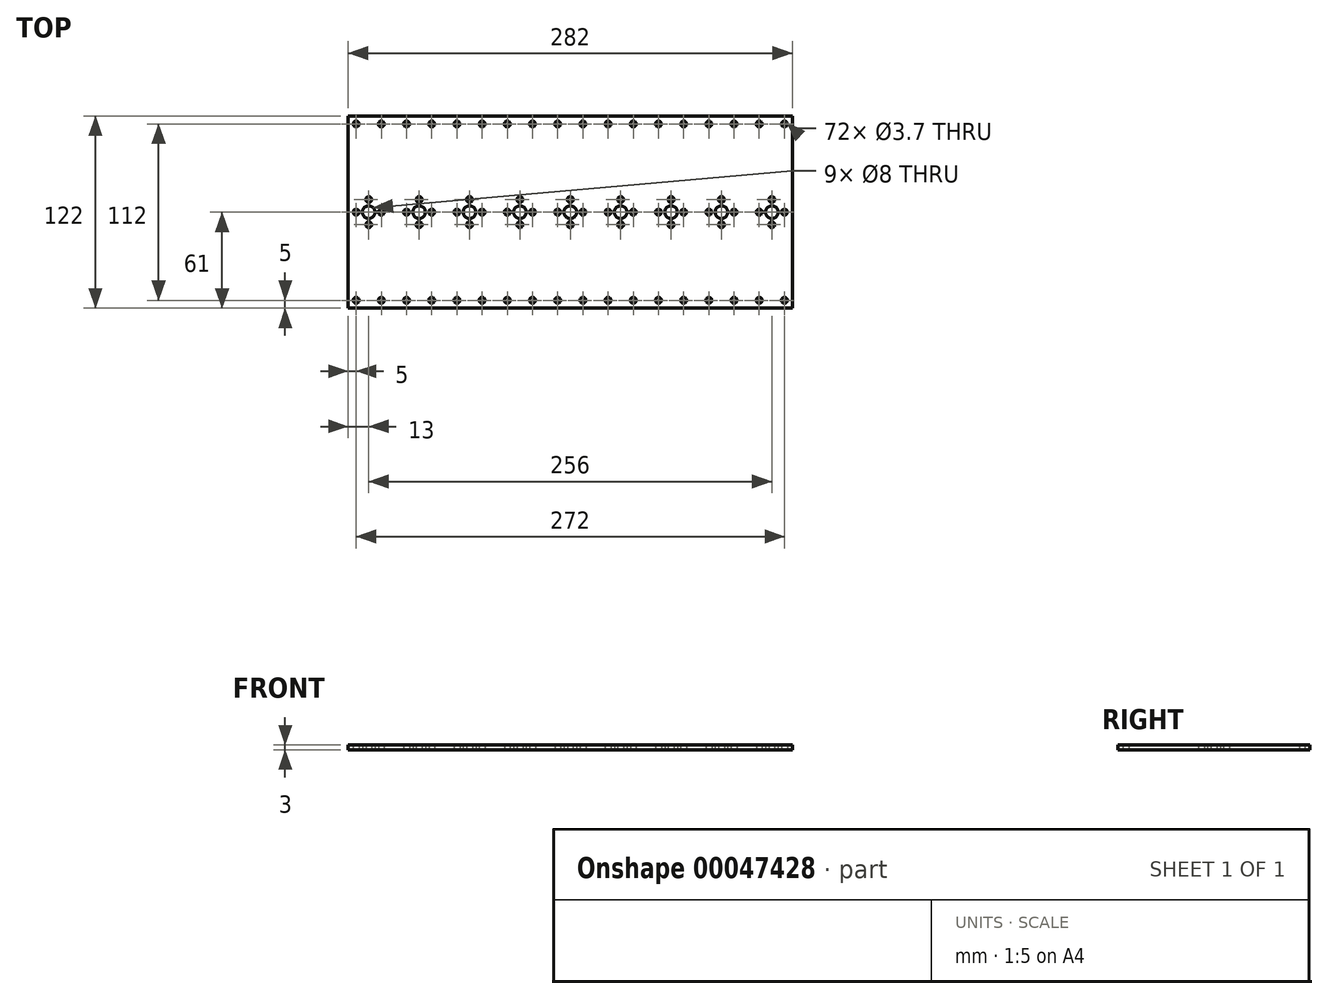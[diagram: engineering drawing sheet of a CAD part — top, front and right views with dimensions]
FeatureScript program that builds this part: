
annotation { "Feature Type Name" : "Feature", "Feature Type Description" : "" }
export const myFeature = defineFeature(function(context is Context, id is Id, definition is map)
    precondition{}
    {
        {
            var Q0;
            Q0=qCreatedBy(makeId("Top.planeOp"),FACE);
            var sketch = newSketch(context, id + "F0", { "sketchPlane" : qUnion([Q0])});
            skLineSegment(sketch, "E0.rect.bottom", {"start": v(-141, -61) * mm, "end": v(141, -61) * mm});
            skLineSegment(sketch, "E0.rect.top", {"start": v(-141, 61) * mm, "end": v(141, 61) * mm});
            skLineSegment(sketch, "E0.rect.left", {"start": v(-141, -61) * mm, "end": v(-141, 61) * mm});
            skLineSegment(sketch, "E0.rect.right", {"start": v(141, -61) * mm, "end": v(141, 61) * mm});
            skPoint(sketch, "E0.rect.middle", {"position": v(0, 0) * mm});
            skCircle(sketch, "E1", {"center": v(0, 0) * mm, "radius": 4 * mm});
            skCircle(sketch, "E2", {"center": v(0, -8) * mm, "radius": 1.85 * mm});
            skCircle(sketch, "E3.1.0", {"center": v(8, 0) * mm, "radius": 1.85 * mm});
            skCircle(sketch, "E3.2.0", {"center": v(0, 8) * mm, "radius": 1.85 * mm});
            skCircle(sketch, "E3.3.0", {"center": v(-8, 0) * mm, "radius": 1.85 * mm});
            skPoint(sketch, "E4.1.0.0", {"position": v(32, 0) * mm});
            skCircle(sketch, "E4.1.0.1", {"center": v(32, 0) * mm, "radius": 4 * mm});
            skCircle(sketch, "E4.1.0.2", {"center": v(40, 0) * mm, "radius": 1.85 * mm});
            skCircle(sketch, "E4.1.0.3", {"center": v(32, 8) * mm, "radius": 1.85 * mm});
            skPoint(sketch, "E4.1.0.4", {"position": v(32, 0) * mm});
            skCircle(sketch, "E4.1.0.5", {"center": v(24, 0) * mm, "radius": 1.85 * mm});
            skCircle(sketch, "E4.1.0.6", {"center": v(32, -8) * mm, "radius": 1.85 * mm});
            skPoint(sketch, "E4.2.0.0", {"position": v(64, 0) * mm});
            skCircle(sketch, "E4.2.0.1", {"center": v(64, 0) * mm, "radius": 4 * mm});
            skCircle(sketch, "E4.2.0.2", {"center": v(72, 0) * mm, "radius": 1.85 * mm});
            skCircle(sketch, "E4.2.0.3", {"center": v(64, 8) * mm, "radius": 1.85 * mm});
            skPoint(sketch, "E4.2.0.4", {"position": v(64, 0) * mm});
            skCircle(sketch, "E4.2.0.5", {"center": v(56, 0) * mm, "radius": 1.85 * mm});
            skCircle(sketch, "E4.2.0.6", {"center": v(64, -8) * mm, "radius": 1.85 * mm});
            skPoint(sketch, "E4.3.0.0", {"position": v(96, 0) * mm});
            skCircle(sketch, "E4.3.0.1", {"center": v(96, 0) * mm, "radius": 4 * mm});
            skCircle(sketch, "E4.3.0.2", {"center": v(104, 0) * mm, "radius": 1.85 * mm});
            skCircle(sketch, "E4.3.0.3", {"center": v(96, 8) * mm, "radius": 1.85 * mm});
            skPoint(sketch, "E4.3.0.4", {"position": v(96, 0) * mm});
            skCircle(sketch, "E4.3.0.5", {"center": v(88, 0) * mm, "radius": 1.85 * mm});
            skCircle(sketch, "E4.3.0.6", {"center": v(96, -8) * mm, "radius": 1.85 * mm});
            skPoint(sketch, "E4.4.0.0", {"position": v(128, 0) * mm});
            skCircle(sketch, "E4.4.0.1", {"center": v(128, 0) * mm, "radius": 4 * mm});
            skCircle(sketch, "E4.4.0.2", {"center": v(136, 0) * mm, "radius": 1.85 * mm});
            skCircle(sketch, "E4.4.0.3", {"center": v(128, 8) * mm, "radius": 1.85 * mm});
            skPoint(sketch, "E4.4.0.4", {"position": v(128, 0) * mm});
            skCircle(sketch, "E4.4.0.5", {"center": v(120, 0) * mm, "radius": 1.85 * mm});
            skCircle(sketch, "E4.4.0.6", {"center": v(128, -8) * mm, "radius": 1.85 * mm});
            skLineSegment(sketch, "E4.direction1", {"start": v(0, 0) * mm, "end": v(32, 0) * mm, "construction": true});
            skCircle(sketch, "E5.1.0.0", {"center": v(-32, 0) * mm, "radius": 4 * mm});
            skCircle(sketch, "E5.1.0.1", {"center": v(-32, -8) * mm, "radius": 1.85 * mm});
            skCircle(sketch, "E5.1.0.2", {"center": v(-24, 0) * mm, "radius": 1.85 * mm});
            skCircle(sketch, "E5.1.0.3", {"center": v(-32, 8) * mm, "radius": 1.85 * mm});
            skCircle(sketch, "E5.1.0.4", {"center": v(-40, 0) * mm, "radius": 1.85 * mm});
            skPoint(sketch, "E5.1.0.5", {"position": v(-32, 0) * mm});
            skPoint(sketch, "E5.1.0.6", {"position": v(-32, 0) * mm});
            skCircle(sketch, "E5.2.0.0", {"center": v(-64, 0) * mm, "radius": 4 * mm});
            skCircle(sketch, "E5.2.0.1", {"center": v(-64, -8) * mm, "radius": 1.85 * mm});
            skCircle(sketch, "E5.2.0.2", {"center": v(-56, 0) * mm, "radius": 1.85 * mm});
            skCircle(sketch, "E5.2.0.3", {"center": v(-64, 8) * mm, "radius": 1.85 * mm});
            skCircle(sketch, "E5.2.0.4", {"center": v(-72, 0) * mm, "radius": 1.85 * mm});
            skPoint(sketch, "E5.2.0.5", {"position": v(-64, 0) * mm});
            skPoint(sketch, "E5.2.0.6", {"position": v(-64, 0) * mm});
            skCircle(sketch, "E5.3.0.0", {"center": v(-96, 0) * mm, "radius": 4 * mm});
            skCircle(sketch, "E5.3.0.1", {"center": v(-96, -8) * mm, "radius": 1.85 * mm});
            skCircle(sketch, "E5.3.0.2", {"center": v(-88, 0) * mm, "radius": 1.85 * mm});
            skCircle(sketch, "E5.3.0.3", {"center": v(-96, 8) * mm, "radius": 1.85 * mm});
            skCircle(sketch, "E5.3.0.4", {"center": v(-104, 0) * mm, "radius": 1.85 * mm});
            skPoint(sketch, "E5.3.0.5", {"position": v(-96, 0) * mm});
            skPoint(sketch, "E5.3.0.6", {"position": v(-96, 0) * mm});
            skCircle(sketch, "E5.4.0.0", {"center": v(-128, 0) * mm, "radius": 4 * mm});
            skCircle(sketch, "E5.4.0.1", {"center": v(-128, -8) * mm, "radius": 1.85 * mm});
            skCircle(sketch, "E5.4.0.2", {"center": v(-120, 0) * mm, "radius": 1.85 * mm});
            skCircle(sketch, "E5.4.0.3", {"center": v(-128, 8) * mm, "radius": 1.85 * mm});
            skCircle(sketch, "E5.4.0.4", {"center": v(-136, 0) * mm, "radius": 1.85 * mm});
            skPoint(sketch, "E5.4.0.5", {"position": v(-128, 0) * mm});
            skPoint(sketch, "E5.4.0.6", {"position": v(-128, 0) * mm});
            skLineSegment(sketch, "E5.direction1", {"start": v(0, 0) * mm, "end": v(-32, 0) * mm, "construction": true});
            skLineSegment(sketch, "E6", {"start": v(-136, 0) * mm, "end": v(-136, -56) * mm, "construction": true});
            skCircle(sketch, "E7", {"center": v(-136, -56) * mm, "radius": 1.85 * mm});
            skCircle(sketch, "E8.1.0.0", {"center": v(-120, -56) * mm, "radius": 1.85 * mm});
            skCircle(sketch, "E8.2.0.0", {"center": v(-104, -56) * mm, "radius": 1.85 * mm});
            skCircle(sketch, "E8.3.0.0", {"center": v(-88, -56) * mm, "radius": 1.85 * mm});
            skCircle(sketch, "E8.4.0.0", {"center": v(-72, -56) * mm, "radius": 1.85 * mm});
            skCircle(sketch, "E8.5.0.0", {"center": v(-56, -56) * mm, "radius": 1.85 * mm});
            skCircle(sketch, "E8.6.0.0", {"center": v(-40, -56) * mm, "radius": 1.85 * mm});
            skCircle(sketch, "E8.7.0.0", {"center": v(-24, -56) * mm, "radius": 1.85 * mm});
            skCircle(sketch, "E8.8.0.0", {"center": v(-8, -56) * mm, "radius": 1.85 * mm});
            skCircle(sketch, "E8.9.0.0", {"center": v(8, -56) * mm, "radius": 1.85 * mm});
            skCircle(sketch, "E8.10.0.0", {"center": v(24, -56) * mm, "radius": 1.85 * mm});
            skCircle(sketch, "E8.11.0.0", {"center": v(40, -56) * mm, "radius": 1.85 * mm});
            skCircle(sketch, "E8.12.0.0", {"center": v(56, -56) * mm, "radius": 1.85 * mm});
            skCircle(sketch, "E8.13.0.0", {"center": v(72, -56) * mm, "radius": 1.85 * mm});
            skCircle(sketch, "E8.14.0.0", {"center": v(88, -56) * mm, "radius": 1.85 * mm});
            skCircle(sketch, "E8.15.0.0", {"center": v(104, -56) * mm, "radius": 1.85 * mm});
            skCircle(sketch, "E8.16.0.0", {"center": v(120, -56) * mm, "radius": 1.85 * mm});
            skCircle(sketch, "E8.17.0.0", {"center": v(136, -56) * mm, "radius": 1.85 * mm});
            skLineSegment(sketch, "E8.direction1", {"start": v(-136, -56) * mm, "end": v(-120, -56) * mm, "construction": true});
            skLineSegment(sketch, "E9", {"start": v(-136, 0) * mm, "end": v(-136, 56) * mm, "construction": true});
            skCircle(sketch, "E10", {"center": v(-136, 56) * mm, "radius": 1.85 * mm});
            skCircle(sketch, "E11.1.0.0", {"center": v(-120, 56) * mm, "radius": 1.85 * mm});
            skCircle(sketch, "E11.2.0.0", {"center": v(-104, 56) * mm, "radius": 1.85 * mm});
            skCircle(sketch, "E11.3.0.0", {"center": v(-88, 56) * mm, "radius": 1.85 * mm});
            skCircle(sketch, "E11.4.0.0", {"center": v(-72, 56) * mm, "radius": 1.85 * mm});
            skCircle(sketch, "E11.5.0.0", {"center": v(-56, 56) * mm, "radius": 1.85 * mm});
            skCircle(sketch, "E11.6.0.0", {"center": v(-40, 56) * mm, "radius": 1.85 * mm});
            skCircle(sketch, "E11.7.0.0", {"center": v(-24, 56) * mm, "radius": 1.85 * mm});
            skCircle(sketch, "E11.8.0.0", {"center": v(-8, 56) * mm, "radius": 1.85 * mm});
            skCircle(sketch, "E11.9.0.0", {"center": v(8, 56) * mm, "radius": 1.85 * mm});
            skCircle(sketch, "E11.10.0.0", {"center": v(24, 56) * mm, "radius": 1.85 * mm});
            skCircle(sketch, "E11.11.0.0", {"center": v(40, 56) * mm, "radius": 1.85 * mm});
            skCircle(sketch, "E11.12.0.0", {"center": v(56, 56) * mm, "radius": 1.85 * mm});
            skCircle(sketch, "E11.13.0.0", {"center": v(72, 56) * mm, "radius": 1.85 * mm});
            skCircle(sketch, "E11.14.0.0", {"center": v(88, 56) * mm, "radius": 1.85 * mm});
            skCircle(sketch, "E11.15.0.0", {"center": v(104, 56) * mm, "radius": 1.85 * mm});
            skCircle(sketch, "E11.16.0.0", {"center": v(120, 56) * mm, "radius": 1.85 * mm});
            skCircle(sketch, "E11.17.0.0", {"center": v(136, 56) * mm, "radius": 1.85 * mm});
            skLineSegment(sketch, "E11.direction1", {"start": v(-136, 56) * mm, "end": v(-120, 56) * mm, "construction": true});
            skSolve(sketch);
        }
        {
            var Q0;
            Q0=makeQuery(id+"F0.imprint","IMPRINT",FACE,{"disambiguationData":[TD([[makeQuery(id+"F0.imprint","IMPRINT",EDGE,{"derivedFrom":sQuery(id+"F0.wireOp",EDGE,"E0.rect.bottom")}),1.0]])]});
            extrude(context, id + "F1", {"entities" : qUnion([Q0]), "depth" : 3 * mm});
        }
    });
